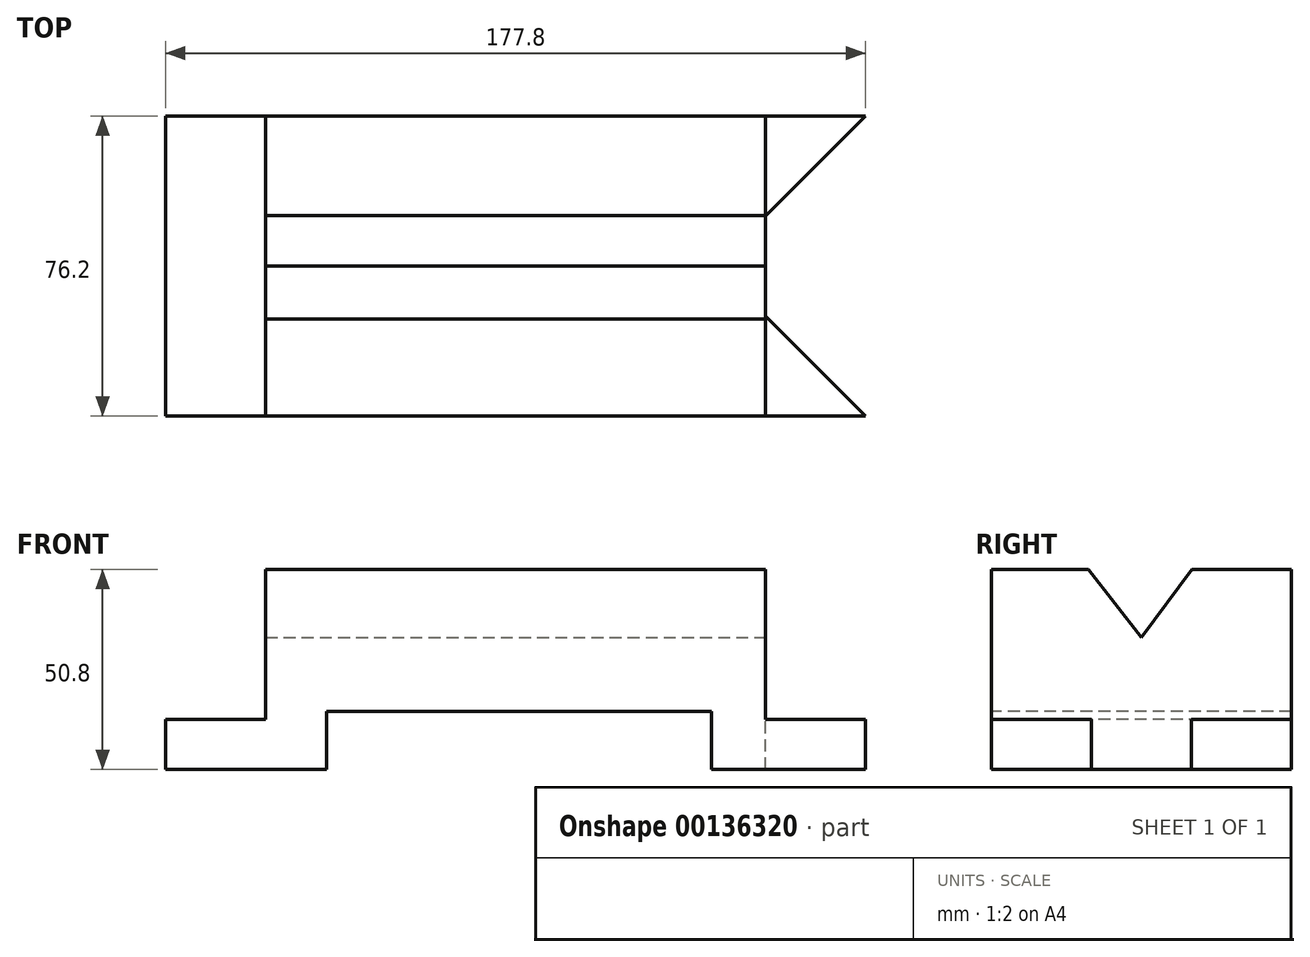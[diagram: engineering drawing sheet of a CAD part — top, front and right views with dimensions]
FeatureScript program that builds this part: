
annotation { "Feature Type Name" : "Feature", "Feature Type Description" : "" }
export const myFeature = defineFeature(function(context is Context, id is Id, definition is map)
    precondition{}
    {
        {
            var Q0;
            Q0=qCreatedBy(makeId("Top.planeOp"),FACE);
            var sketch = newSketch(context, id + "F0", { "sketchPlane" : qUnion([Q0])});
            skLineSegment(sketch, "E0.bottom", {"start": v(78.24, 38.1) * mm, "end": v(-74.16, 38.1) * mm});
            skLineSegment(sketch, "E0.top", {"start": v(78.24, -38.1) * mm, "end": v(-74.16, -38.1) * mm});
            skLineSegment(sketch, "E0.left", {"start": v(78.24, 38.1) * mm, "end": v(78.24, -38.1) * mm});
            skLineSegment(sketch, "E0.right", {"start": v(-74.16, 38.1) * mm, "end": v(-74.16, -38.1) * mm});
            skPoint(sketch, "E0.middle", {"position": v(2.04, 0) * mm});
            skSolve(sketch);
        }
        {
            var Q0;
            Q0=makeQuery(id+"F0.imprint","IMPRINT",FACE,{"disambiguationData":[TD([[makeQuery(id+"F0.imprint","IMPRINT",EDGE,{"derivedFrom":sQuery(id+"F0.wireOp",EDGE,"E0.bottom")}),1.0]])]});
            extrude(context, id + "F1", {"entities" : qUnion([Q0]), "depth" : 50.8 * mm});
        }
        {
            var Q0;
            Q0=makeQuery(id+"F1.opExtrude","CAP_FACE",FACE,{"disambiguationData":[OSD([sQuery(id+"F0.wireOp",EDGE,"E0.bottom"),sQuery(id+"F0.wireOp",EDGE,"E0.top"),sQuery(id+"F0.wireOp",EDGE,"E0.left"),sQuery(id+"F0.wireOp",EDGE,"E0.right")])],"isStart":false});
            var sketch = newSketch(context, id + "F2", { "sketchPlane" : qUnion([Q0])});
            skLineSegment(sketch, "E1", {"start": v(78.24, 38.1) * mm, "end": v(52.84, 38.1) * mm});
            skLineSegment(sketch, "E2", {"start": v(52.84, 38.1) * mm, "end": v(52.84, 12.7) * mm});
            skLineSegment(sketch, "E3", {"start": v(52.84, 12.7) * mm, "end": v(78.24, 38.1) * mm});
            skLineSegment(sketch, "E4", {"start": v(78.24, -38.1) * mm, "end": v(52.84, -38.1) * mm});
            skLineSegment(sketch, "E5", {"start": v(52.84, -38.1) * mm, "end": v(52.84, -12.7) * mm});
            skLineSegment(sketch, "E6", {"start": v(78.24, -38.1) * mm, "end": v(52.84, -12.7) * mm});
            skLineSegment(sketch, "E7", {"start": v(52.84, 12.7) * mm, "end": v(52.84, -12.7) * mm});
            skSolve(sketch);
        }
        {
            var Q0;
            Q0=makeQuery(id+"F2.imprint","IMPRINT",FACE,{"disambiguationData":[TD([[makeQuery(id+"F2.imprint","IMPRINT",EDGE,{"derivedFrom":sQuery(id+"F2.wireOp",EDGE,"E3")}),-1.0]])]});
            extrude(context, id + "F3", {"entities" : qUnion([Q0]), "operationType" : NewBodyOperationType.REMOVE, "endBound" : BoundingType.THROUGH_ALL, "oppositeDirection" : true, "depth" : 25.4 * mm});
        }
        {
            var Q0;
            Q0=makeQuery(id+"F2.imprint","IMPRINT",FACE,{"disambiguationData":[TD([[makeQuery(id+"F2.imprint","IMPRINT",EDGE,{"derivedFrom":sQuery(id+"F2.wireOp",EDGE,"E1")}),1.0]])]});
            extrude(context, id + "F4", {"entities" : qUnion([Q0]), "operationType" : NewBodyOperationType.REMOVE, "oppositeDirection" : true, "depth" : 38.1 * mm});
        }
        {
            var Q0;
            Q0=makeQuery(id+"F2.imprint","IMPRINT",FACE,{"disambiguationData":[TD([[makeQuery(id+"F2.imprint","IMPRINT",EDGE,{"derivedFrom":sQuery(id+"F2.wireOp",EDGE,"E4")}),-1.0]])]});
            extrude(context, id + "F5", {"entities" : qUnion([Q0]), "operationType" : NewBodyOperationType.REMOVE, "oppositeDirection" : true, "depth" : 38.1 * mm});
        }
        {
            var Q0;
            Q0=makeQuery(id+"F5.boolean.opBoolean","MERGE",FACE,{"derivedFrom":[makeQuery(id+"F4.boolean.opBoolean","MERGE",FACE,{"derivedFrom":[makeQuery(id+"F3.boolean.opBoolean","COPY",FACE,{"derivedFrom":makeQuery(id+"F3.opExtrude","SWEPT_FACE",FACE,{"disambiguationData":[OSD([sQuery(id+"F2.wireOp",EDGE,"E7")])]})}),makeQuery(id+"F4.opExtrude","SWEPT_FACE",FACE,{"disambiguationData":[OSD([sQuery(id+"F2.wireOp",EDGE,"E2")])]})]}),makeQuery(id+"F5.opExtrude","SWEPT_FACE",FACE,{"disambiguationData":[OSD([sQuery(id+"F2.wireOp",EDGE,"E5")])]})]});
            var sketch = newSketch(context, id + "F6", { "sketchPlane" : qUnion([Q0])});
            skLineSegment(sketch, "E8", {"start": v(-13.4, 50.8) * mm, "end": v(0, 33.52) * mm});
            skLineSegment(sketch, "E9", {"start": v(0, 33.52) * mm, "end": v(12.81, 50.8) * mm});
            skLineSegment(sketch, "E10", {"start": v(-13.4, 50.8) * mm, "end": v(12.81, 50.8) * mm});
            skSolve(sketch);
        }
        {
            var Q0;
            Q0=makeQuery(id+"F6.imprint","IMPRINT",FACE,{"disambiguationData":[TD([[makeQuery(id+"F6.imprint","IMPRINT",EDGE,{"derivedFrom":sQuery(id+"F6.wireOp",EDGE,"E8")}),1.0]])]});
            extrude(context, id + "F7", {"entities" : qUnion([Q0]), "operationType" : NewBodyOperationType.REMOVE, "endBound" : BoundingType.THROUGH_ALL, "oppositeDirection" : true, "depth" : 25.4 * mm});
        }
        {
            var Q0;
            Q0=makeQuery(id+"F1.opExtrude","SWEPT_FACE",FACE,{"disambiguationData":[OSD([sQuery(id+"F0.wireOp",EDGE,"E0.top")])]});
            var sketch = newSketch(context, id + "F8", { "sketchPlane" : qUnion([Q0])});
            skLineSegment(sketch, "E11.bottom", {"start": v(39.06, 0) * mm, "end": v(-58.68, 0) * mm});
            skLineSegment(sketch, "E11.top", {"start": v(39.06, 14.75) * mm, "end": v(-58.68, 14.75) * mm});
            skLineSegment(sketch, "E11.left", {"start": v(39.06, 0) * mm, "end": v(39.06, 14.75) * mm});
            skLineSegment(sketch, "E11.right", {"start": v(-58.68, 0) * mm, "end": v(-58.68, 14.75) * mm});
            skSolve(sketch);
        }
        {
            var Q0;
            Q0=qSketchRegion(id+"F8",true);
            extrude(context, id + "F9", {"entities" : qUnion([Q0]), "operationType" : NewBodyOperationType.REMOVE, "endBound" : BoundingType.THROUGH_ALL, "oppositeDirection" : true, "depth" : 25.4 * mm});
        }
        {
            var Q0;
            Q0=makeQuery(id+"F1.opExtrude","SWEPT_FACE",FACE,{"disambiguationData":[OSD([sQuery(id+"F0.wireOp",EDGE,"E0.right")])]});
            var sketch = newSketch(context, id + "F10", { "sketchPlane" : qUnion([Q0])});
            skLineSegment(sketch, "E12.bottom", {"start": v(-38.1, 12.7) * mm, "end": v(38.1, 12.7) * mm});
            skLineSegment(sketch, "E12.top", {"start": v(-38.1, 0) * mm, "end": v(38.1, 0) * mm});
            skLineSegment(sketch, "E12.left", {"start": v(-38.1, 12.7) * mm, "end": v(-38.1, 0) * mm});
            skLineSegment(sketch, "E12.right", {"start": v(38.1, 12.7) * mm, "end": v(38.1, 0) * mm});
            skSolve(sketch);
        }
        {
            var Q0;
            Q0=makeQuery(id+"F10.imprint","IMPRINT",FACE,{"disambiguationData":[TD([[makeQuery(id+"F10.imprint","IMPRINT",EDGE,{"derivedFrom":sQuery(id+"F10.wireOp",EDGE,"E12.bottom")}),-1.0]])]});
            extrude(context, id + "F11", {"entities" : qUnion([Q0]), "operationType" : NewBodyOperationType.ADD, "depth" : 25.4 * mm});
        }
    });
